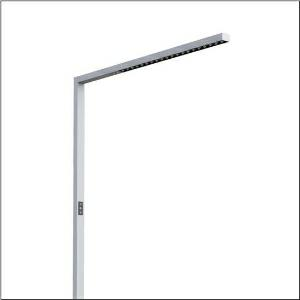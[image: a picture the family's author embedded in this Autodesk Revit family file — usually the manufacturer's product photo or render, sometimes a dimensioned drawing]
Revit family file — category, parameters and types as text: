
# Revit family: silica_r__31_floor_51my52fa3cs_6121
name_source: partatom
category: Lighting Fixtures
units: mm (PartAtom-declared; Revit-internal decimal feet)

## family parameters
Cut with Voids When Loaded = No
Host = Face
Light Source = No
Part Type = Normal
Room Calculation Point = No
Round Connector Dimension = Use Diameter
Shared = No

## types (1)
- Silica® 31 Floor (1 x LED, 10300 lm, 75 W, 3000K)
    Apparent Load = 75 VA
    CIE Flux Codes = 86 100 100 24 100
    Color Rendering = 80
    Color Temperature = 3000K
    Default Elevation = 1800 mm
    Description = Silica® 31 Floor, floorstanding luminaire, secondary optical cover: cover panel, of PMMA, light emission: direct/indirect distribution, primary light characteristic: symmetric, installation type: not mounted, LED, rated luminous flux: 10.300lm, luminous efficacy: 137lm/W, light colour: 830, colour temperature: 3000K, control gear: Touchdim, daylight-dependent control, with cable with plug, mains connection: 230V, AC, 50Hz, connection cable pre-assembled, rated input power: 75W, luminaire head, of aluminium, metallic grey (RAL 9006), length: 1.203mm, width: 52mm, supporting column, angular, of aluminium, metallic grey (RAL 9006), baseplate, of steel, metallic grey (RAL 9006), protection rating (complete): IP20, insulation class (complete): insulation class I (protective earthing), certification: CE, permissible operating ambient temperature: -20..+40°C, standard: EN 50419, packaging unit: 1 piece
    Height = 36 mm
    Lamp = 1 x LED
    Lamp Light Flux = 10300 lm
    Lamp Power = 75 W
    Lamp count = 1
    Length = 1203 mm
    Luminous efficacy = 137 lm/W
    Manufacturer = Siteco
    ModVariant = No
    Model = 51MY52FA3CS
    Mounting Place = Floor
    Mounting Type = Freestanding
    Number of Poles = 1
    OnlyDefault = Yes
    Power Factor = 1
    Product Name = Silica® 31 Floor
    Product group = floorstanding luminaire
    ProductGroupID = 1302
    Protection Class = Protection class I
    Protection Degree = IP 20
    RLX_Detail_Level = 1
    RLX_Emergency_Light_Flux = 0 lm
    RLX_Emergency_Type = 0
    RLX_Emergency_Type_DB = No
    RlxData = <blob elided: 19569 chars, md5=8e544689>
    Socket = socket
    Standby Power = 0 W
    System Light Flux = 10300 lm
    System Power = 75 W
    Type Comments = Product without accessories
    Type Image = l_1275303.jpg
    URL = http://relux.com
    VarID = ---
    Voltage = 0 V
    Weight = 0.00 kg
    Width = 52 mm  [stored 0.170604 ft]

note: [stored X ft] marks values corroborated as IEEE doubles in the binary element streams (Revit-internal decimal feet)

## geometry (parser evidence)
native form markers: Blend x4, Sweep x15
no freeform markers — native parametric forms only
